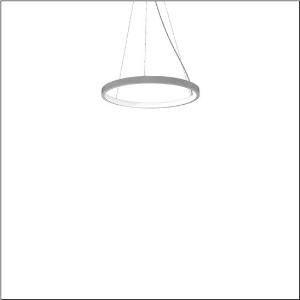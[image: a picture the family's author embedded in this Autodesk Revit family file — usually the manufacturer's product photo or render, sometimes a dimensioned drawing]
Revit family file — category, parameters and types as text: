
# Revit family: silica_r__21_ring-i_5pjbi1d1204a_31f3
name_source: partatom
category: Lighting Fixtures
units: mm (PartAtom-declared; Revit-internal decimal feet)

## family parameters
Cut with Voids When Loaded = No
Host = Face
Light Source = No
Part Type = Normal
Room Calculation Point = No
Round Connector Dimension = Use Diameter
Shared = No

## types (1)
- Silica® 21 Ring-I (1 x LED, 3430 lm, 60 W, 3000K)
    Apparent Load = 60 VA
    CIE Flux Codes = 22 48 76 50 101
    Color Rendering = 80
    Color Temperature = 3000K
    Default Elevation = 1800 mm
    Description = Silica® 21 Ring-I, suspended luminaire, of PMMA, frosted, light emission: inner ring side luminous distribution, primary light characteristic: symmetric, installation type: suspended mounting, LED, rated luminous flux: 3.430lm, luminous efficacy: 57lm/W, light colour: 830, colour temperature: 3000K, with terminal, 5-pole, mains connection: 230V, AC/DC, 0/50..60Hz, rated input power: 60W, housing, of extruded aluminium section, metallic grey (RAL 9006), diameter: 610mm, ceiling canopy, metallic grey (RAL 9006), protection rating (lamp compartment): IP40, insulation class (complete): insulation class I (protective earthing), certification: CE, impact resistance: IK02, permissible operating ambient temperature: 0..+35°C, packaging unit: 1 piece
    Height = 48 mm  [stored 0.15748 ft]
    Lamp = 1 x LED
    Lamp Light Flux = 3430 lm
    Lamp Power = 60 W
    Lamp count = 1
    Length = 610 mm
    Luminous efficacy = 57 lm/W
    Manufacturer = Siteco
    ModVariant = No
    Model = 5PJBI1D1204A
    Mounting Place = Ceiling
    Mounting Type = Pendant
    Number of Poles = 1
    OnlyDefault = Yes
    Power Factor = 1
    Product Name = Silica® 21 Ring-I
    Product group = suspended luminaire
    ProductGroupID = 904
    Protection Class = Protection class I
    Protection Degree = Degree of protection
    RLX_Detail_Level = 1
    RLX_Emergency_Light_Flux = 0 lm
    RLX_Emergency_Type = 0
    RLX_Emergency_Type_DB = No
    RlxData = <blob elided: 11477 chars, md5=2f37f2c5>
    Socket = socket
    Standby Power = 0 W
    System Light Flux = 3430 lm
    System Power = 60 W
    Type Comments = Product without accessories
    Type Image = l_1251750.jpg
    URL = http://relux.com
    VarID = ---
    Voltage = 0 V
    Weight = 0.00 kg
    Width = 0 mm  [stored 0 ft]

note: [stored X ft] marks values corroborated as IEEE doubles in the binary element streams (Revit-internal decimal feet)

## geometry (parser evidence)
native form markers: Sweep x12
no freeform markers — native parametric forms only
